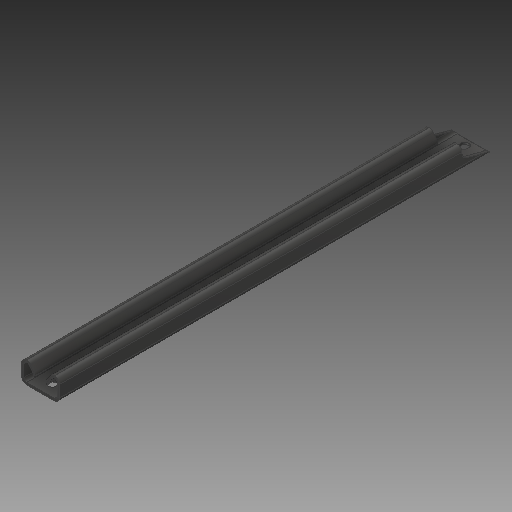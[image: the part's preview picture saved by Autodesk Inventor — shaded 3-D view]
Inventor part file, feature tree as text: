
AUTODESK INVENTOR PART (.ipt)
format: ipt  version: 2019 (Build 230136000, 136)  size: 422,912 bytes
history: native  units: mm
features: sketch x5, sheet_metal_op x3, other x3, fillet x2, hole x2, extrude x1, pattern_linear x1
ambient origin geometry x8: Origin, YZ Plane, XZ Plane, XY Plane, X Axis, Y Axis, Z Axis, Center Point
bodies: Solid1 (feature_tree)
feature tree (17):
  sheet_metal_op  "Contour Flange1"
  extrude  "Extrusion1"  Depth=2.3mm
  fillet  "Fillet1"  Radius=2.3mm
  fillet  "Fillet2"  Radius=1.15mm
  pattern_linear  "Rectangular Pattern1"  Spacing1=0.5mm  [1 undecoded]
  sketch  "Sketch5"  dims[d28=2.3mm d29=0.5mm d30=9.2mm d31=2.3mm d32=2.3mm d37=455.0mm d38=30.0mm d39=23.5mm d40=75.0deg d41=3.5mm d42=10.0mm d43=0.0mm d44=6.0mm d45=2.0mm d47=20.0mm d49=10.0mm d51=20.0mm d53=10.0mm d54=5.075mm d55=5.075mm d56=8.150021mm d58=4.075008mm d59=413.202mm d60=21.05mm d61=10.0mm d62=10.0mm d63=13.0mm d64=2.3mm d65=0.0mm d66=8.0mm d67=5.0mm d70=1.0mm d71=4.0mm d72=407.0mm d73=2.3mm d74=0.0mm d75=270.0mm d77=10.0mm d78=24.5mm d79=376.0mm d80=21.0mm d81=8.0mm d82=6.0mm d83=4.0mm d84=2.0mm d85=90.0deg d86=2.3mm d87=20.594885mm d88=10.0mm d89=6.0mm d90=4.0mm d91=2.0mm d92=90.0deg d93=2.3mm d94=20.594885mm]
  hole  "Hole1"  [1 undecoded]
  hole  "Hole2"  [1 undecoded]
  sketch  "Sketch1"  dims[d0=40.0mm d1=20.0mm d2=2.3mm d4=2.3mm d13=2.5mm d14=2.5mm d15=23.0mm d21=5.3mm d22=2.3mm d23=2.3mm d24=1.15mm]
  other  "Plate1"
  sheet_metal_op  "Bend1"
  sheet_metal_op  "Corner1"
  sketch  "Sketch2"  dims[d25=4.6mm]
  sketch  "Sketch3"  dims[d26=2.3mm]
  sketch  "Sketch4"  dims[d27=455.0mm]
  other  "Cut1"
  other  "Cut2"
note: 3 required parameter values undecoded (feature->parameter linkage not recoverable at this tier; creation-order binding heuristic only, values carry confidence <= 0.55)
